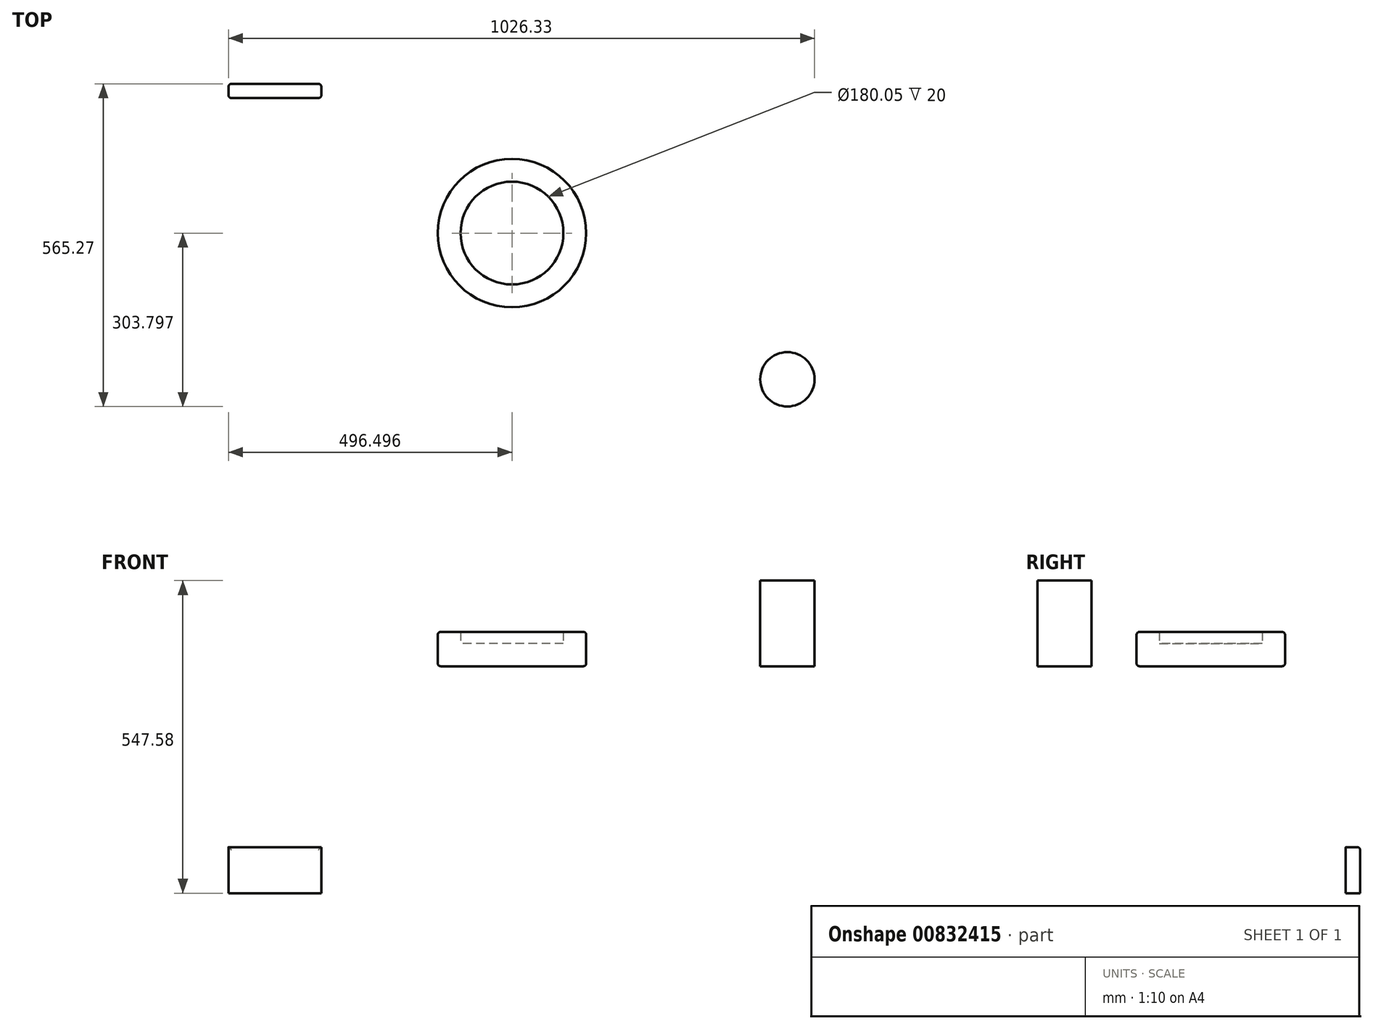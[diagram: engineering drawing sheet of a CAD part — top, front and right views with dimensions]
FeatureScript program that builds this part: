
annotation { "Feature Type Name" : "Feature", "Feature Type Description" : "" }
export const myFeature = defineFeature(function(context is Context, id is Id, definition is map)
    precondition{}
    {
        {
            var Q0;
            Q0=qCreatedBy(makeId("Top.planeOp"),FACE);
            var sketch = newSketch(context, id + "F0", { "sketchPlane" : qUnion([Q0])});
            skCircle(sketch, "E0", {"center": v(-170.26, -261.47) * mm, "radius": 130.03 * mm});
            skSolve(sketch);
        }
        {
            var Q0;
            Q0=makeQuery(id+"F0.imprint","IMPRINT",FACE,{"disambiguationData":[TD([[makeQuery(id+"F0.imprint","IMPRINT",EDGE,{"derivedFrom":sQuery(id+"F0.wireOp",EDGE,"E0")}),1.0]])]});
            extrude(context, id + "F1", {"entities" : qUnion([Q0]), "depth" : 60 * mm, "offsetDistance" : 25 * mm});
        }
        {
            var Q0;
            Q0=makeQuery(id+"F1.opExtrude","CAP_FACE",FACE,{"disambiguationData":[OSD([sQuery(id+"F0.wireOp",EDGE,"E0")])],"isStart":false});
            shell(context, id + "F2", {"entities" : qUnion([Q0]), "thickness" : 40 * mm});
        }
        {
            var Q0;
            Q0=makeQuery(id+"F1.opExtrude","CAP_EDGE",EDGE,{"disambiguationData":[OSD([sQuery(id+"F0.wireOp",EDGE,"E0")])],"isStart":false});
            fillet(context, id + "F3", {"entities" : qUnion([Q0]), "radius" : 5 * mm, "tangentPropagation" : true, "allowEdgeOverflow" : false});
        }
        {
            var Q0;
            Q0=qCreatedBy(makeId("Top.planeOp"),FACE);
            var sketch = newSketch(context, id + "F4", { "sketchPlane" : qUnion([Q0])});
            skCircle(sketch, "E1", {"center": v(312, -517.7) * mm, "radius": 47.57 * mm});
            skSolve(sketch);
        }
        {
            var Q0;
            Q0=makeQuery(id+"F4.imprint","IMPRINT",FACE,{"disambiguationData":[TD([[makeQuery(id+"F4.imprint","IMPRINT",EDGE,{"derivedFrom":sQuery(id+"F4.wireOp",EDGE,"E1")}),1.0]])]});
            extrude(context, id + "F5", {"entities" : qUnion([Q0]), "depth" : 150 * mm, "offsetDistance" : 25 * mm});
        }
        {
            var Q0;
            Q0=qCreatedBy(makeId("Front.planeOp"),FACE);
            var sketch = newSketch(context, id + "F6", { "sketchPlane" : qUnion([Q0])});
            skLineSegment(sketch, "E2.bottom", {"start": v(-666.76, -316.96) * mm, "end": v(-504.26, -316.96) * mm});
            skLineSegment(sketch, "E2.top", {"start": v(-666.76, -397.58) * mm, "end": v(-504.26, -397.58) * mm});
            skLineSegment(sketch, "E2.left", {"start": v(-666.76, -316.96) * mm, "end": v(-666.76, -397.58) * mm});
            skLineSegment(sketch, "E2.right", {"start": v(-504.26, -316.96) * mm, "end": v(-504.26, -397.58) * mm});
            skSolve(sketch);
        }
        {
            var Q0;
            Q0=makeQuery(id+"F6.imprint","IMPRINT",FACE,{"disambiguationData":[TD([[makeQuery(id+"F6.imprint","IMPRINT",EDGE,{"derivedFrom":sQuery(id+"F6.wireOp",EDGE,"E2.bottom")}),-1.0]])]});
            extrude(context, id + "F7", {"entities" : qUnion([Q0]), "depth" : 25 * mm, "offsetDistance" : 25 * mm});
        }
        {
            var Q0;
            Q0=makeQuery(id+"F7.opExtrude","CAP_EDGE",EDGE,{"disambiguationData":[OSD([sQuery(id+"F6.wireOp",EDGE,"E2.bottom")])],"isStart":true});
            var Q1;
            Q1=makeQuery(id+"F7.opExtrude","CAP_EDGE",EDGE,{"disambiguationData":[OSD([sQuery(id+"F6.wireOp",EDGE,"E2.left")])],"isStart":false});
            var Q2;
            Q2=makeQuery(id+"F7.opExtrude","CAP_EDGE",EDGE,{"disambiguationData":[OSD([sQuery(id+"F6.wireOp",EDGE,"E2.right")])],"isStart":false});
            var Q3;
            Q3=makeQuery(id+"F7.opExtrude","CAP_EDGE",EDGE,{"disambiguationData":[OSD([sQuery(id+"F6.wireOp",EDGE,"E2.left")])],"isStart":true});
            var Q4;
            Q4=makeQuery(id+"F7.opExtrude","CAP_EDGE",EDGE,{"disambiguationData":[OSD([sQuery(id+"F6.wireOp",EDGE,"E2.right")])],"isStart":true});
            var Q5;
            Q5=makeQuery(id+"F1.opExtrude","CAP_FACE",FACE,{"disambiguationData":[OSD([sQuery(id+"F0.wireOp",EDGE,"E0")])],"isStart":true});
            fillet(context, id + "F8", {"entities" : qUnion([Q0, Q1, Q2, Q3, Q4, Q5]), "radius" : 5 * mm, "tangentPropagation" : true, "allowEdgeOverflow" : false});
        }
    });
